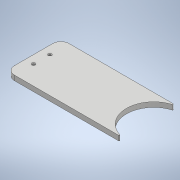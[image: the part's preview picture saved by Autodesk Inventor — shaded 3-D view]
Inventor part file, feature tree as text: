
AUTODESK INVENTOR PART (.ipt)
format: ipt  version: 2020 (Build 240168000, 168)  size: 127,488 bytes
history: native  units: mm
features: fillet x2, extrude x1, hole x1, sketch x1
ambient origin geometry x8: Origin, YZ Plane, XZ Plane, XY Plane, X Axis, Y Axis, Z Axis, Center Point
bodies: Body1 (feature_tree)
feature tree (5):
  extrude  "Выдавливание3"  Depth=11.75mm
  fillet  "Сопряжение3"  Radius=2.1mm
  fillet  "Сопряжение4"  Radius=40.0mm
  hole  "Отверстие1"  [1 undecoded]
  sketch  "Эскиз6"
note: 1 required parameter value undecoded (feature->parameter linkage not recoverable at this tier; creation-order binding heuristic only, values carry confidence <= 0.55)
